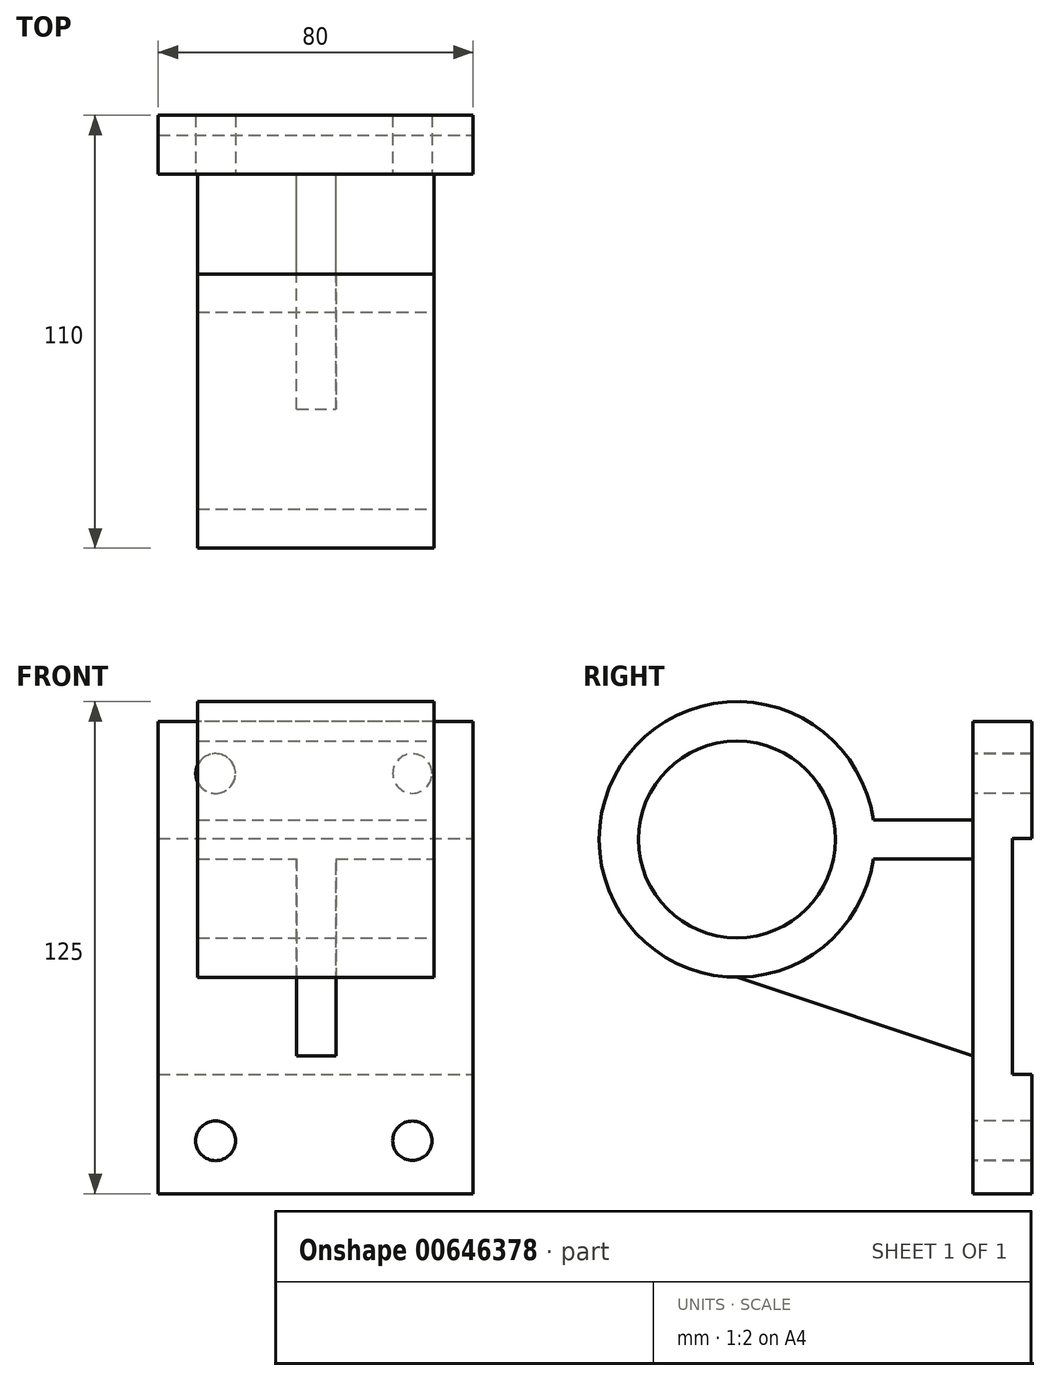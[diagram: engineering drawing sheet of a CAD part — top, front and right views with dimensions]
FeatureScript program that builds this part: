
annotation { "Feature Type Name" : "Feature", "Feature Type Description" : "" }
export const myFeature = defineFeature(function(context is Context, id is Id, definition is map)
    precondition{}
    {
        {
            var Q0;
            Q0=qCreatedBy(makeId("Front.planeOp"),FACE);
            var sketch = newSketch(context, id + "F0", { "sketchPlane" : qUnion([Q0])});
            skLineSegment(sketch, "E0", {"start": v(-63.18, 61.07) * mm, "end": v(-63.18, -58.93) * mm});
            skLineSegment(sketch, "E1", {"start": v(-63.18, -58.93) * mm, "end": v(16.82, -58.93) * mm});
            skLineSegment(sketch, "E2", {"start": v(16.82, -58.93) * mm, "end": v(16.82, 61.07) * mm});
            skLineSegment(sketch, "E3", {"start": v(16.82, 61.07) * mm, "end": v(-63.18, 61.07) * mm});
            skSolve(sketch);
        }
        {
            var Q0;
            Q0 = qSketchRegion(id + "F0", true);
            extrude(context, id + "F1", {"entities" : qUnion([Q0]), "depth" : 15 * mm, "offsetDistance" : 25 * mm});
        }
        {
            var Q0;
            Q0=makeQuery(id+"F1.opExtrude","CAP_FACE",FACE,{"disambiguationData":[OSD([sQuery(id+"F0.wireOp",EDGE,"E0"),sQuery(id+"F0.wireOp",EDGE,"E1"),sQuery(id+"F0.wireOp",EDGE,"E2"),sQuery(id+"F0.wireOp",EDGE,"E3")])],"isStart":false});
            var sketch = newSketch(context, id + "F2", { "sketchPlane" : qUnion([Q0])});
            skLineSegment(sketch, "E4", {"start": v(-53.18, 36.07) * mm, "end": v(6.82, 36.07) * mm});
            skLineSegment(sketch, "E5", {"start": v(6.82, 36.07) * mm, "end": v(6.82, 26.07) * mm});
            skLineSegment(sketch, "E6", {"start": v(6.82, 26.07) * mm, "end": v(-53.18, 26.07) * mm});
            skLineSegment(sketch, "E7", {"start": v(-53.18, 26.07) * mm, "end": v(-53.18, 36.07) * mm});
            skLineSegment(sketch, "E8", {"start": v(-27.74, 26.07) * mm, "end": v(-27.74, -23.93) * mm});
            skLineSegment(sketch, "E9", {"start": v(-27.74, -23.93) * mm, "end": v(-17.74, -23.93) * mm});
            skLineSegment(sketch, "E10", {"start": v(-17.74, -23.93) * mm, "end": v(-17.74, 26.07) * mm});
            skSolve(sketch);
        }
        {
            var Q0;
            Q0=makeQuery(id+"F2.imprint","IMPRINT",FACE,{"disambiguationData":[TD([[makeQuery(id+"F2.imprint","IMPRINT",EDGE,{"derivedFrom":sQuery(id+"F2.wireOp",EDGE,"E4")}),-1.0]])]});
            extrude(context, id + "F3", {"entities" : qUnion([Q0]), "operationType" : NewBodyOperationType.ADD, "depth" : 60 * mm, "offsetDistance" : 25 * mm});
        }
        {
            var Q0;
            Q0=makeQuery(id+"F3.opExtrude","SWEPT_FACE",FACE,{"disambiguationData":[OSD([sQuery(id+"F2.wireOp",EDGE,"E5")])]});
            var sketch = newSketch(context, id + "F4", { "sketchPlane" : qUnion([Q0])});
            skCircle(sketch, "E11", {"center": v(-75, 31.07) * mm, "radius": 35 * mm});
            skCircle(sketch, "E12", {"center": v(-75, 31.07) * mm, "radius": 25 * mm});
            skSolve(sketch);
        }
        {
            var Q0;
            Q0 = qSketchRegion(id + "F4", true);
            extrude(context, id + "F5", {"entities" : qUnion([Q0]), "operationType" : NewBodyOperationType.ADD, "oppositeDirection" : true, "depth" : 60 * mm, "offsetDistance" : 25 * mm});
        }
        {
            var Q0;
            Q0=makeQuery(id+"F5.boolean.opBoolean","MERGE",FACE,{"derivedFrom":[makeQuery(id+"F3.opExtrude","SWEPT_FACE",FACE,{"disambiguationData":[OSD([sQuery(id+"F2.wireOp",EDGE,"E5")])]}),makeQuery(id+"F5.opExtrude","CAP_FACE",FACE,{"disambiguationData":[OSD([sQuery(id+"F4.wireOp",EDGE,"E11"),sQuery(id+"F4.wireOp",EDGE,"E12")])],"isStart":true})]});
            var sketch = newSketch(context, id + "F6", { "sketchPlane" : qUnion([Q0])});
            skCircle(sketch, "E13", {"center": v(-75, 31.07) * mm, "radius": 25 * mm});
            skSolve(sketch);
        }
        {
            var Q0;
            Q0 = qSketchRegion(id + "F6", true);
            extrude(context, id + "F7", {"entities" : qUnion([Q0]), "operationType" : NewBodyOperationType.REMOVE, "oppositeDirection" : true, "depth" : 72.2 * mm, "offsetDistance" : 25 * mm});
        }
        {
            var Q0;
            Q0=makeQuery(id+"F1.opExtrude","CAP_FACE",FACE,{"disambiguationData":[OSD([sQuery(id+"F0.wireOp",EDGE,"E0"),sQuery(id+"F0.wireOp",EDGE,"E1"),sQuery(id+"F0.wireOp",EDGE,"E2"),sQuery(id+"F0.wireOp",EDGE,"E3")])],"isStart":false});
            var sketch = newSketch(context, id + "F8", { "sketchPlane" : qUnion([Q0])});
            skLineSegment(sketch, "E14", {"start": v(-28, 26.07) * mm, "end": v(-28, -23.93) * mm});
            skLineSegment(sketch, "E15", {"start": v(-28, -23.93) * mm, "end": v(-18, -23.93) * mm});
            skLineSegment(sketch, "E16", {"start": v(-18, -23.93) * mm, "end": v(-18, 26.07) * mm});
            skLineSegment(sketch, "E17", {"start": v(-18, 26.07) * mm, "end": v(-28, 26.07) * mm});
            skSolve(sketch);
        }
        {
            var Q0;
            Q0 = qSketchRegion(id + "F8", true);
            extrude(context, id + "F9", {"entities" : qUnion([Q0]), "operationType" : NewBodyOperationType.ADD, "depth" : 59.7 * mm, "offsetDistance" : 25 * mm});
        }
        {
            var Q0;
            {var subQ1=sQuery(id+"F8.wireOp",EDGE,"E14");Q0=makeQuery(id+"F9.boolean.opBoolean","SPLIT",FACE,{"disambiguationData":[TD([makeQuery(id+"F3.opExtrude","SWEPT_FACE",FACE,{"disambiguationData":[OSD([sQuery(id+"F2.wireOp",EDGE,"E6")])]})])],"derivedFrom":makeQuery(id+"F9.opExtrude","SWEPT_FACE",FACE,{"disambiguationData":[OSD([subQ1])]})});}
            var sketch = newSketch(context, id + "F10", { "sketchPlane" : qUnion([Q0])});
            skLineSegment(sketch, "E18", {"start": v(74.7, -3.93) * mm, "end": v(15, -23.93) * mm});
            skLineSegment(sketch, "E19", {"start": v(15, -23.93) * mm, "end": v(56.14, -39.03) * mm});
            skLineSegment(sketch, "E20", {"start": v(56.14, -39.03) * mm, "end": v(87.14, -23.93) * mm});
            skLineSegment(sketch, "E21", {"start": v(87.14, -23.93) * mm, "end": v(74.7, -3.93) * mm});
            skSolve(sketch);
        }
        {
            var Q0;
            Q0 = qSketchRegion(id + "F10", true);
            extrude(context, id + "F11", {"entities" : qUnion([Q0]), "operationType" : NewBodyOperationType.REMOVE, "oppositeDirection" : true, "depth" : 25 * mm, "offsetDistance" : 25 * mm});
        }
        {
            var Q0;
            Q0=makeQuery(id+"F1.opExtrude","CAP_FACE",FACE,{"disambiguationData":[OSD([sQuery(id+"F0.wireOp",EDGE,"E0"),sQuery(id+"F0.wireOp",EDGE,"E1"),sQuery(id+"F0.wireOp",EDGE,"E2"),sQuery(id+"F0.wireOp",EDGE,"E3")])],"isStart":false});
            var sketch = newSketch(context, id + "F12", { "sketchPlane" : qUnion([Q0])});
            skCircle(sketch, "E22", {"center": v(-48.62, -45.5) * mm, "radius": 5.05 * mm});
            skCircle(sketch, "E23", {"center": v(1.38, -45.5) * mm, "radius": 5 * mm});
            skCircle(sketch, "E24.0.1.0", {"center": v(-48.62, 47.8) * mm, "radius": 5.05 * mm});
            skCircle(sketch, "E24.0.1.1", {"center": v(1.38, 47.8) * mm, "radius": 5 * mm});
            skLineSegment(sketch, "E24.direction1", {"start": v(-48.62, -45.5) * mm, "end": v(-23.62, -45.5) * mm, "construction": true});
            skLineSegment(sketch, "E24.direction2", {"start": v(-48.62, -45.5) * mm, "end": v(-48.62, 47.8) * mm, "construction": true});
            skSolve(sketch);
        }
        {
            var Q0;
            Q0 = qSketchRegion(id + "F12", true);
            extrude(context, id + "F13", {"entities" : qUnion([Q0]), "operationType" : NewBodyOperationType.REMOVE, "oppositeDirection" : true, "depth" : 39.5 * mm, "offsetDistance" : 25 * mm});
        }
        {
            var Q0;
            Q0=makeQuery(id+"F1.opExtrude","SWEPT_FACE",FACE,{"disambiguationData":[OSD([sQuery(id+"F0.wireOp",EDGE,"E2")])]});
            var sketch = newSketch(context, id + "F14", { "sketchPlane" : qUnion([Q0])});
            skLineSegment(sketch, "E25", {"start": v(0, -28.65) * mm, "end": v(-5, -28.65) * mm});
            skLineSegment(sketch, "E26", {"start": v(-5, -28.65) * mm, "end": v(-5, 31.35) * mm});
            skLineSegment(sketch, "E27", {"start": v(-5, 31.35) * mm, "end": v(0, 31.35) * mm});
            skLineSegment(sketch, "E28", {"start": v(0, 31.35) * mm, "end": v(0, -28.65) * mm});
            skSolve(sketch);
        }
        {
            var Q0;
            Q0 = qSketchRegion(id + "F14", true);
            extrude(context, id + "F15", {"entities" : qUnion([Q0]), "operationType" : NewBodyOperationType.REMOVE, "oppositeDirection" : true, "depth" : 85.5 * mm, "offsetDistance" : 25 * mm});
        }
        {
            var Q0;
            Q0=makeQuery(id+"F5.boolean.opBoolean","MERGE",FACE,{"derivedFrom":[makeQuery(id+"F3.opExtrude","SWEPT_FACE",FACE,{"disambiguationData":[OSD([sQuery(id+"F2.wireOp",EDGE,"E7")])]}),makeQuery(id+"F5.opExtrude","CAP_FACE",FACE,{"disambiguationData":[OSD([sQuery(id+"F4.wireOp",EDGE,"E11"),sQuery(id+"F4.wireOp",EDGE,"E12")])],"isStart":false})]});
            var sketch = newSketch(context, id + "F16", { "sketchPlane" : qUnion([Q0])});
            skCircle(sketch, "E29", {"center": v(75, 31.07) * mm, "radius": 25 * mm});
            skSolve(sketch);
        }
        {
            var Q0;
            Q0 = qSketchRegion(id + "F16", true);
            extrude(context, id + "F17", {"entities" : qUnion([Q0]), "operationType" : NewBodyOperationType.REMOVE, "oppositeDirection" : true, "depth" : 91.3 * mm, "offsetDistance" : 25 * mm});
        }
    });
